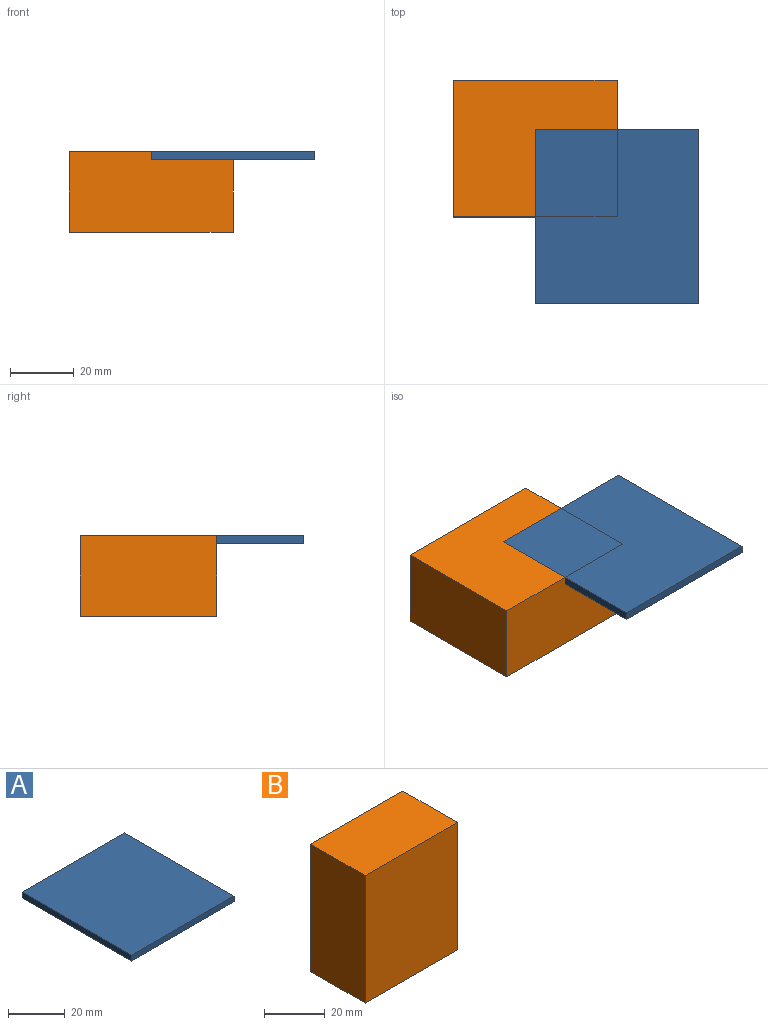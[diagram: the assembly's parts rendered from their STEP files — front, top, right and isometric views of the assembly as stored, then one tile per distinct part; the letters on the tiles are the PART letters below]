
ASSEMBLY  parts=2 mates=1
PART A: 6 faces, bbox 51.3x54.8x2.5 mm
  f0: plane 51.35x2.54mm, normal (0,1,0), area 130.4mm2, adj f1,f3,f4,f5
  f1: plane 54.78x2.54mm, normal (-1,0,0), area 139.2mm2, adj f0,f2,f4,f5
  f2: plane 51.35x2.54mm, normal (0,-1,0), area 130.4mm2, adj f1,f3,f4,f5
  f3: plane 54.78x2.54mm, normal (1,0,0), area 139.2mm2, adj f0,f2,f4,f5
  f4: plane 54.78x51.35mm, normal (0,0,1), area 2813mm2, adj f0,f1,f2,f3
  f5: plane 54.78x51.35mm, normal (0,0,-1), area 2813mm2, adj f0,f1,f2,f3
PART B: 6 faces, bbox 43x25.4x51.5 mm
  f0: plane 51.54x25.4mm, normal (-1,0,0), area 1309mm2, adj f1,f3,f4,f5
  f1: plane 43.04x25.4mm, normal (0,0,-1), area 1093.2mm2, adj f0,f2,f4,f5
  f2: plane 51.54x25.4mm, normal (1,0,0), area 1309mm2, adj f1,f3,f4,f5
  f3: plane 43.04x25.4mm, normal (0,0,1), area 1093.2mm2, adj f0,f2,f4,f5
  f4: plane 51.54x43.04mm, normal (0,-1,0), area 2218.1mm2, adj f0,f1,f2,f3
  f5: plane 51.54x43.04mm, normal (0,1,0), area 2218.1mm2, adj f0,f1,f2,f3
PLACE A rot(axis=(0,0,1),0deg) t=(29.82,68.2,12.38)mm
PLACE B rot(axis=(-0.58,-0.58,0.58),120deg) t=(55.5,40.8,-10.48)mm
MATE parallel B.f4 <-> A.f4  axis (0,0,1) through (55.5,40.8,14.92)mm
